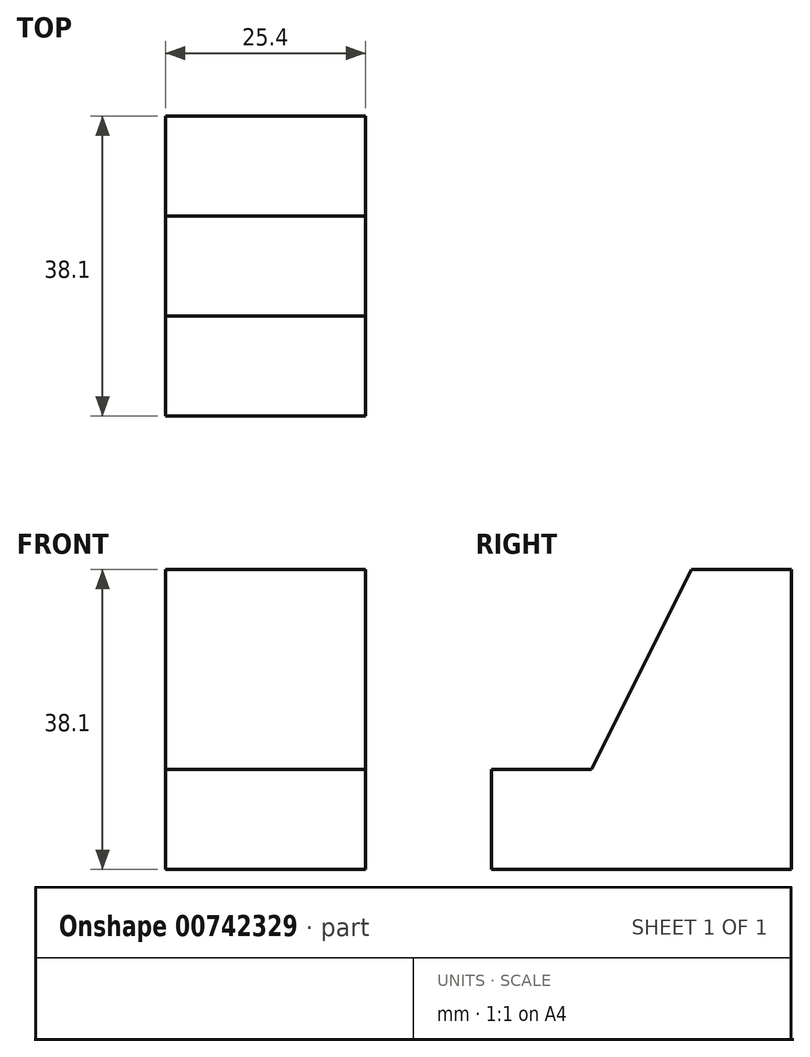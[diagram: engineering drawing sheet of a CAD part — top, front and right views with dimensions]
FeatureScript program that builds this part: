
annotation { "Feature Type Name" : "Feature", "Feature Type Description" : "" }
export const myFeature = defineFeature(function(context is Context, id is Id, definition is map)
    precondition{}
    {
        {
            var Q0;
            Q0=qCreatedBy(makeId("Right.planeOp"),FACE);
            var sketch = newSketch(context, id + "F0", { "sketchPlane" : qUnion([Q0])});
            skLineSegment(sketch, "E0", {"start": v(0, 0) * mm, "end": v(38.1, 0) * mm});
            skLineSegment(sketch, "E1", {"start": v(38.1, 0) * mm, "end": v(38.1, 38.1) * mm});
            skLineSegment(sketch, "E2", {"start": v(38.1, 38.1) * mm, "end": v(25.4, 38.1) * mm});
            skLineSegment(sketch, "E3", {"start": v(25.4, 38.1) * mm, "end": v(12.7, 12.7) * mm});
            skLineSegment(sketch, "E4", {"start": v(12.7, 12.7) * mm, "end": v(0, 12.7) * mm});
            skLineSegment(sketch, "E5", {"start": v(0, 12.7) * mm, "end": v(0, 0) * mm});
            skSolve(sketch);
        }
        {
            var Q0;
            Q0 = qSketchRegion(id + "F0", true);
            extrude(context, id + "F1", {"entities" : qUnion([Q0]), "depth" : 25.4 * mm, "offsetDistance" : 25.4 * mm});
        }
    });
